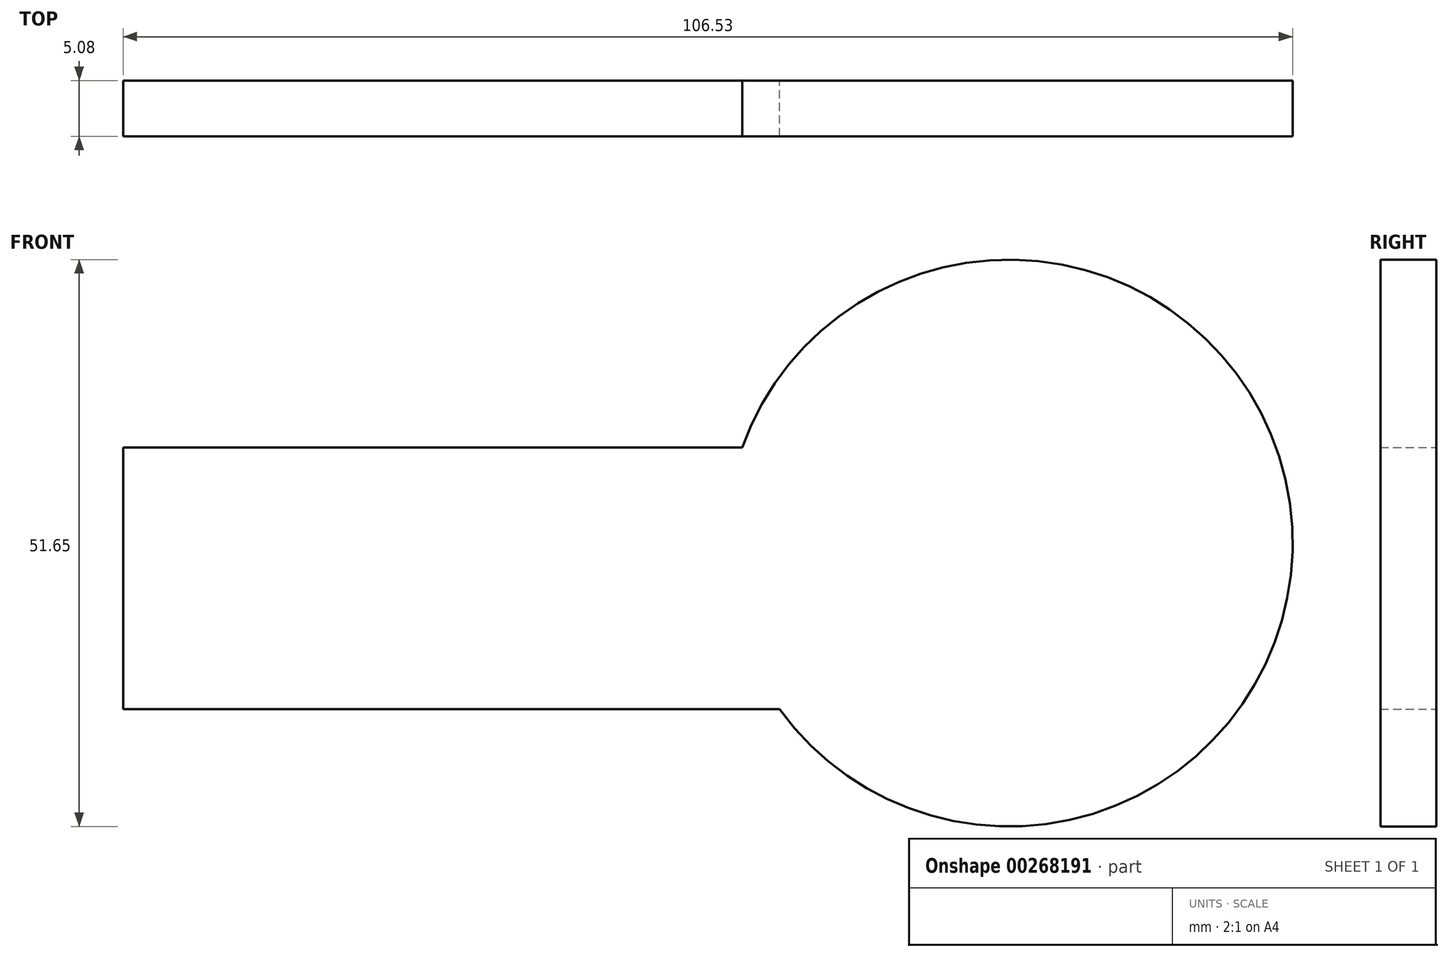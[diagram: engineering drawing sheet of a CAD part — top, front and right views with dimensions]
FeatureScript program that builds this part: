
annotation { "Feature Type Name" : "Feature", "Feature Type Description" : "" }
export const myFeature = defineFeature(function(context is Context, id is Id, definition is map)
    precondition{}
    {
        {
            var Q0;
            Q0=qCreatedBy(makeId("Front.planeOp"),FACE);
            var sketch = newSketch(context, id + "F0", { "sketchPlane" : qUnion([Q0])});
            skLineSegment(sketch, "E0.bottom", {"start": v(-3.36, 33.6) * mm, "end": v(-59.75, 33.6) * mm});
            skLineSegment(sketch, "E0.top", {"start": v(0.03, 9.75) * mm, "end": v(-59.75, 9.75) * mm});
            skLineSegment(sketch, "E0.right", {"start": v(-59.75, 33.6) * mm, "end": v(-59.75, 9.75) * mm});
            skArc(sketch, "E1", {"start": v(0.03, 9.75) * mm, "mid": v(46.52, 28.53) * mm, "end": v(-3.36, 33.6) * mm});
            skSolve(sketch);
        }
        {
            var Q0;
            Q0=makeQuery(id+"F0.imprint","IMPRINT",FACE,{"disambiguationData":[TD([[makeQuery(id+"F0.imprint","IMPRINT",EDGE,{"derivedFrom":sQuery(id+"F0.wireOp",EDGE,"E0.bottom")}),1.0]])]});
            var sketch = newSketch(context, id + "F1", { "sketchPlane" : qUnion([Q0])});
            skSolve(sketch);
        }
        {
            var Q0;
            Q0=makeQuery(id+"F1.imprint","IMPRINT",FACE,{"disambiguationData":[TD([[makeQuery(id+"F1.imprint","IMPRINT",EDGE,{"derivedFrom":makeQuery(id+"F0.imprint","IMPRINT",EDGE,{"derivedFrom":sQuery(id+"F0.wireOp",EDGE,"E0.bottom")})}),1.0]])]});
            extrude(context, id + "F2", {"entities" : qUnion([Q0]), "depth" : 5.08 * mm});
        }
    });
